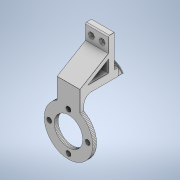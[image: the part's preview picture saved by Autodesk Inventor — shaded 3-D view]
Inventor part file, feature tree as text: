
AUTODESK INVENTOR PART (.ipt)
format: ipt  version: 2021 (Build 250183000, 183)  size: 1,098,240 bytes
history: native  units: mm
features: extrude x8, sketch x6, projected_geometry x6, other x3, delete_face x3, chamfer x1, fillet x1
ambient origin geometry x8: Origin, YZ Plane, XZ Plane, XY Plane, X Axis, Y Axis, Z Axis, Center Point
bodies: Solid1 (feature_tree)
feature tree (28):
  other  "franka_gripper_connection3.ipt"
  extrude  "Extrusion1"  Depth=0.394mm
  delete_face  "Delete Face1"
  delete_face  "Delete Face2"
  extrude  "Extrusion5"  Depth=8.0mm
  sketch  "Sketch9"  dims[d14=42.0mm d15=0.0mm d16=4.3mm]
  extrude  "Extrusion6"  Depth=42.0mm
  extrude  "Extrusion7"  Depth=7.2mm
  delete_face  "Delete Face3"
  extrude  "Extrusion8"  Depth=5.6mm
  extrude  "Extrusion9"  Depth=0.2mm
  sketch  "Sketch12"  dims[d22=3.928mm d23=7.0mm d24=7.0mm d25=3.2mm d26=0.0mm d27=0.0mm d28=0.0mm d29=22.0mm d30=0.0mm d34=0.0mm d35=0.0mm d36=17.0mm d37=18.676mm d38=3.5mm d39=3.5mm d40=90.0deg d41=18.676mm d42=3.5mm d43=18.676mm d44=6.0mm d45=0.0mm d46=17.5mm d47=18.676mm d48=18.676mm d49=5.0mm d50=0.0mm d51=1.5mm d52=2.0mm d53=45.0deg d54=0.2mm d31=0.5mm d32=0.872665mm]
  extrude  "Extrusion10"  Depth=0.2mm
  extrude  "Extrusion11"  Depth=0.2mm TaperAngle=0.0deg
  chamfer  "Chamfer1"  [1 undecoded]
  fillet  "Fillet2"  Radius=22.0mm
  other  "Solid1::franka_gripper_connection3.ipt"
  other  "TaggingFeature1"
  sketch  "Sketch4"  dims[d0=10.0mm d3=0.394mm]
  projected_geometry  "Projected Loop1"
  sketch  "Sketch8"  dims[d1=3.0mm d2=0.0mm d13=8.0mm]
  projected_geometry  "Projected Loop5"
  projected_geometry  "Projected Loop6"
  sketch  "Sketch10"  dims[d17=4.3mm d19=7.2mm]
  projected_geometry  "Projected Loop7"
  sketch  "Sketch11"  dims[d20=7.2mm d21=5.6mm]
  projected_geometry  "Projected Loop8"
  projected_geometry  "Projected Loop9"
note: 1 required parameter value undecoded (feature->parameter linkage not recoverable at this tier; creation-order binding heuristic only, values carry confidence <= 0.55)
